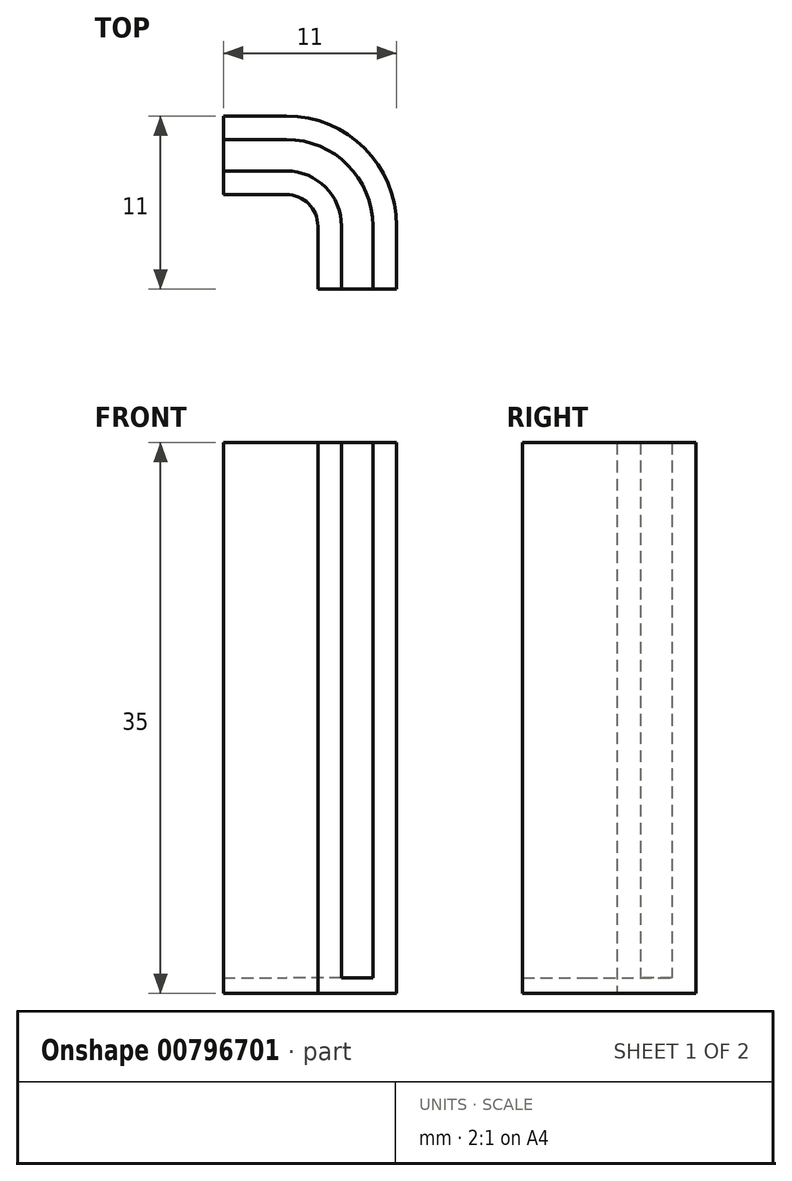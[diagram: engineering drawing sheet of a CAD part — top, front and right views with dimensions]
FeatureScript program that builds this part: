
annotation { "Feature Type Name" : "Feature", "Feature Type Description" : "" }
export const myFeature = defineFeature(function(context is Context, id is Id, definition is map)
    precondition{}
    {
        {
            assignVariable(context, id + "F0", {"name" : "bracket_height", "anyValue" : 35});
        }
        {
            var Q0;
            Q0=qCreatedBy(makeId("Top.planeOp"),FACE);
            var sketch = newSketch(context, id + "F1", { "sketchPlane" : qUnion([Q0])});
            skCircle(sketch, "E0", {"center": v(0, 0) * mm, "radius": 2 * mm});
            skCircle(sketch, "E1", {"center": v(0, 0) * mm, "radius": 3.5 * mm});
            skCircle(sketch, "E2", {"center": v(0, 0) * mm, "radius": 5.5 * mm});
            skCircle(sketch, "E3", {"center": v(0, 0) * mm, "radius": 7 * mm});
            skLineSegment(sketch, "E4", {"start": v(0, 0) * mm, "end": v(0, 7) * mm, "construction": true});
            skLineSegment(sketch, "E5", {"start": v(0, 0) * mm, "end": v(7, 0) * mm, "construction": true});
            skPoint(sketch, "E6", {"position": v(0, 3.5) * mm});
            skPoint(sketch, "E7", {"position": v(0, 5.5) * mm});
            skPoint(sketch, "E8", {"position": v(0, 7) * mm});
            skPoint(sketch, "E9", {"position": v(3.5, 0) * mm});
            skPoint(sketch, "E10", {"position": v(5.5, 0) * mm});
            skPoint(sketch, "E11", {"position": v(0, 2) * mm});
            skPoint(sketch, "E12", {"position": v(2, 0) * mm});
            skLineSegment(sketch, "E13", {"start": v(0, 2) * mm, "end": v(-4, 2) * mm});
            skLineSegment(sketch, "E14", {"start": v(2, 0) * mm, "end": v(2, -4) * mm});
            skPoint(sketch, "E15", {"position": v(7, 0) * mm});
            skLineSegment(sketch, "E16", {"start": v(0, 3.5) * mm, "end": v(-4, 3.5) * mm});
            skLineSegment(sketch, "E17", {"start": v(0, 5.5) * mm, "end": v(-4, 5.5) * mm});
            skLineSegment(sketch, "E18", {"start": v(0, 7) * mm, "end": v(-4, 7) * mm});
            skLineSegment(sketch, "E19", {"start": v(3.5, 0) * mm, "end": v(3.5, -4) * mm});
            skLineSegment(sketch, "E20", {"start": v(5.5, 0) * mm, "end": v(5.5, -4) * mm});
            skLineSegment(sketch, "E21", {"start": v(7, 0) * mm, "end": v(7, -4) * mm});
            skLineSegment(sketch, "E22", {"start": v(-4, 7) * mm, "end": v(-4, 2) * mm});
            skLineSegment(sketch, "E23", {"start": v(2, -4) * mm, "end": v(7, -4) * mm});
            skSolve(sketch);
        }
        {
            var Q0;
            {var subQ0=sQuery(id+"F1.wireOp",EDGE,"E17");var subQ1=sQuery(id+"F1.wireOp",EDGE,"E2");var subQ2=makeQuery(id+"F1.imprint","INTERSECT",VERTEX,{"derivedFrom":[subQ1,subQ0]});Q0=makeQuery(id+"F1.imprint","IMPRINT",FACE,{"disambiguationData":[TD([[makeQuery(id+"F1.imprint","IMPRINT",EDGE,{"disambiguationData":[TD([[subQ2,-1.0]])],"derivedFrom":subQ1}),-1.0]])]});}
            var Q1;
            {var subQ0=sQuery(id+"F1.wireOp",EDGE,"E16");var subQ1=sQuery(id+"F1.wireOp",EDGE,"E2");var subQ2=makeQuery(id+"F1.imprint","INTERSECT",VERTEX,{"derivedFrom":[subQ1,subQ0]});Q1=makeQuery(id+"F1.imprint","IMPRINT",FACE,{"disambiguationData":[TD([[makeQuery(id+"F1.imprint","IMPRINT",EDGE,{"disambiguationData":[TD([[subQ2,-1.0]])],"derivedFrom":subQ1}),-1.0]])]});}
            var Q2;
            {var subQ0=sQuery(id+"F1.wireOp",EDGE,"E14");var subQ1=sQuery(id+"F1.wireOp",EDGE,"E2");var subQ2=makeQuery(id+"F1.imprint","INTERSECT",VERTEX,{"derivedFrom":[subQ1,subQ0]});Q2=makeQuery(id+"F1.imprint","IMPRINT",FACE,{"disambiguationData":[TD([[makeQuery(id+"F1.imprint","IMPRINT",EDGE,{"disambiguationData":[TD([[subQ2,-1.0]])],"derivedFrom":subQ1}),-1.0]])]});}
            var Q3;
            {var subQ0=sQuery(id+"F1.wireOp",EDGE,"E20");var subQ1=sQuery(id+"F1.wireOp",EDGE,"E2");var subQ2=makeQuery(id+"F1.imprint","INTERSECT",VERTEX,{"derivedFrom":[subQ1,subQ0]});Q3=makeQuery(id+"F1.imprint","IMPRINT",FACE,{"disambiguationData":[TD([[makeQuery(id+"F1.imprint","IMPRINT",EDGE,{"disambiguationData":[TD([[subQ2,1.0]])],"derivedFrom":subQ1}),-1.0]])]});}
            var Q4;
            {var subQ0=sQuery(id+"F1.wireOp",EDGE,"E18");Q4=makeQuery(id+"F1.imprint","IMPRINT",FACE,{"disambiguationData":[TD([[makeQuery(id+"F1.imprint","IMPRINT",EDGE,{"derivedFrom":subQ0}),1.0]])]});}
            var Q5;
            {var subQ0=sQuery(id+"F1.wireOp",EDGE,"E13");var subQ1=sQuery(id+"F1.wireOp",EDGE,"E3");var subQ2=makeQuery(id+"F1.imprint","INTERSECT",VERTEX,{"derivedFrom":[subQ1,subQ0]});Q5=makeQuery(id+"F1.imprint","IMPRINT",FACE,{"disambiguationData":[TD([[makeQuery(id+"F1.imprint","IMPRINT",EDGE,{"disambiguationData":[TD([[subQ2,1.0]])],"derivedFrom":subQ1}),-1.0]])]});}
            var Q6;
            {var subQ0=sQuery(id+"F1.wireOp",EDGE,"E14");var subQ1=sQuery(id+"F1.wireOp",EDGE,"E3");var subQ2=makeQuery(id+"F1.imprint","INTERSECT",VERTEX,{"derivedFrom":[subQ1,subQ0]});Q6=makeQuery(id+"F1.imprint","IMPRINT",FACE,{"disambiguationData":[TD([[makeQuery(id+"F1.imprint","IMPRINT",EDGE,{"disambiguationData":[TD([[subQ2,-1.0]])],"derivedFrom":subQ1}),-1.0]])]});}
            var Q7;
            {var subQ0=sQuery(id+"F1.wireOp",EDGE,"E21");Q7=makeQuery(id+"F1.imprint","IMPRINT",FACE,{"disambiguationData":[TD([[makeQuery(id+"F1.imprint","IMPRINT",EDGE,{"derivedFrom":subQ0}),-1.0]])]});}
            var Q8;
            {var subQ0=sQuery(id+"F1.wireOp",EDGE,"E17");var subQ1=sQuery(id+"F1.wireOp",EDGE,"E3");var subQ2=makeQuery(id+"F1.imprint","INTERSECT",VERTEX,{"derivedFrom":[subQ1,subQ0]});Q8=makeQuery(id+"F1.imprint","IMPRINT",FACE,{"disambiguationData":[TD([[makeQuery(id+"F1.imprint","IMPRINT",EDGE,{"disambiguationData":[TD([[subQ2,-1.0]])],"derivedFrom":subQ1}),-1.0]])]});}
            var Q9;
            {var subQ0=sQuery(id+"F1.wireOp",EDGE,"E19");var subQ1=sQuery(id+"F1.wireOp",EDGE,"E3");var subQ2=makeQuery(id+"F1.imprint","INTERSECT",VERTEX,{"derivedFrom":[subQ1,subQ0]});Q9=makeQuery(id+"F1.imprint","IMPRINT",FACE,{"disambiguationData":[TD([[makeQuery(id+"F1.imprint","IMPRINT",EDGE,{"disambiguationData":[TD([[subQ2,-1.0]])],"derivedFrom":subQ1}),-1.0]])]});}
            var Q10;
            {var subQ0=sQuery(id+"F1.wireOp",EDGE,"E16");var subQ1=sQuery(id+"F1.wireOp",EDGE,"E1");var subQ2=makeQuery(id+"F1.imprint","INTERSECT",VERTEX,{"derivedFrom":[subQ1,subQ0]});Q10=makeQuery(id+"F1.imprint","IMPRINT",FACE,{"disambiguationData":[TD([[makeQuery(id+"F1.imprint","IMPRINT",EDGE,{"disambiguationData":[TD([[subQ2,-1.0]])],"derivedFrom":subQ1}),-1.0]])]});}
            var Q11;
            {var subQ0=sQuery(id+"F1.wireOp",EDGE,"E19");var subQ1=sQuery(id+"F1.wireOp",EDGE,"E1");var subQ2=makeQuery(id+"F1.imprint","INTERSECT",VERTEX,{"derivedFrom":[subQ1,subQ0]});Q11=makeQuery(id+"F1.imprint","IMPRINT",FACE,{"disambiguationData":[TD([[makeQuery(id+"F1.imprint","IMPRINT",EDGE,{"disambiguationData":[TD([[subQ2,1.0]])],"derivedFrom":subQ1}),-1.0]])]});}
            var Q12;
            {var subQ2=sQuery(id+"F1.wireOp",EDGE,"E13");var subQ6=sQuery(id+"F1.wireOp",EDGE,"E0");var subQ9=makeQuery(id+"F1.imprint","INTERSECT",VERTEX,{"derivedFrom":[subQ6,subQ2]});Q12=makeQuery(id+"F1.imprint","IMPRINT",FACE,{"disambiguationData":[TD([[makeQuery(id+"F1.imprint","IMPRINT",EDGE,{"disambiguationData":[TD([[subQ9,1.0]])],"derivedFrom":subQ6}),-1.0]])]});}
            var Q13;
            {var subQ5=sQuery(id+"F1.wireOp",EDGE,"E16");var subQ6=sQuery(id+"F1.wireOp",EDGE,"E1");var subQ7=makeQuery(id+"F1.imprint","INTERSECT",VERTEX,{"derivedFrom":[subQ6,subQ5]});Q13=makeQuery(id+"F1.imprint","IMPRINT",FACE,{"disambiguationData":[TD([[makeQuery(id+"F1.imprint","IMPRINT",EDGE,{"disambiguationData":[TD([[subQ7,1.0]])],"derivedFrom":subQ6}),-1.0]])]});}
            var Q14;
            {var subQ5=sQuery(id+"F1.wireOp",EDGE,"E17");var subQ7=sQuery(id+"F1.wireOp",EDGE,"E2");var subQ8=makeQuery(id+"F1.imprint","INTERSECT",VERTEX,{"derivedFrom":[subQ7,subQ5]});Q14=makeQuery(id+"F1.imprint","IMPRINT",FACE,{"disambiguationData":[TD([[makeQuery(id+"F1.imprint","IMPRINT",EDGE,{"disambiguationData":[TD([[subQ8,1.0]])],"derivedFrom":subQ7}),-1.0]])]});}
            extrude(context, id + "F2", {"entities" : qUnion([Q0, Q1, Q2, Q3, Q4, Q5, Q6, Q7, Q8, Q9, Q10, Q11, Q12, Q13, Q14]), "depth" : 1 * mm, "offsetDistance" : 25 * mm});
        }
        {
            var Q0;
            {var subQ8=sQuery(id+"F1.wireOp",EDGE,"E17");Q0=makeQuery(id+"F1.imprint","IMPRINT",FACE,{"disambiguationData":[TD([[makeQuery(id+"F1.imprint","IMPRINT",EDGE,{"derivedFrom":subQ8}),-1.0]])]});}
            var Q1;
            {var subQ0=sQuery(id+"F1.wireOp",EDGE,"E18");Q1=makeQuery(id+"F1.imprint","IMPRINT",FACE,{"disambiguationData":[TD([[makeQuery(id+"F1.imprint","IMPRINT",EDGE,{"derivedFrom":subQ0}),1.0]])]});}
            var Q2;
            {var subQ0=sQuery(id+"F1.wireOp",EDGE,"E21");Q2=makeQuery(id+"F1.imprint","IMPRINT",FACE,{"disambiguationData":[TD([[makeQuery(id+"F1.imprint","IMPRINT",EDGE,{"derivedFrom":subQ0}),-1.0]])]});}
            var Q3;
            {var subQ0=sQuery(id+"F1.wireOp",EDGE,"E19");Q3=makeQuery(id+"F1.imprint","IMPRINT",FACE,{"disambiguationData":[TD([[makeQuery(id+"F1.imprint","IMPRINT",EDGE,{"derivedFrom":subQ0}),-1.0]])]});}
            var Q4;
            {var subQ2=sQuery(id+"F1.wireOp",EDGE,"E13");var subQ4=sQuery(id+"F1.wireOp",EDGE,"E0");var subQ5=makeQuery(id+"F1.imprint","INTERSECT",VERTEX,{"derivedFrom":[subQ4,subQ2]});Q4=makeQuery(id+"F1.imprint","IMPRINT",FACE,{"disambiguationData":[TD([[makeQuery(id+"F1.imprint","IMPRINT",EDGE,{"disambiguationData":[TD([[subQ5,1.0]])],"derivedFrom":subQ4}),-1.0]])]});}
            var Q5;
            {var subQ0=sQuery(id+"F1.wireOp",EDGE,"E16");Q5=makeQuery(id+"F1.imprint","IMPRINT",FACE,{"disambiguationData":[TD([[makeQuery(id+"F1.imprint","IMPRINT",EDGE,{"derivedFrom":subQ0}),1.0]])]});}
            extrude(context, id + "F3", {"entities" : qUnion([Q0, Q1, Q2, Q3, Q4, Q5]), "operationType" : NewBodyOperationType.ADD, "depth" : (getVariable(context, 'bracket_height')) * mm, "offsetDistance" : 25 * mm});
        }
    });
